# Revit family: 0052239 Lighting Fixture_Sylvania_Rana LED 600x600-DALI dimmable-4000K_Ceiling Recessed
name_source: partatom
category: Lighting Fixtures
revit_build: Autodesk Revit 2015 (Build: 20140606_1530(x64)
units: mm (PartAtom-declared; Revit-internal decimal feet)

## types (1)
- RANA LED 600 CM+P 2*LL DA 4K
    Accessory Material = Aluminum_Sylvania_RanaLED_White
    Apparent Load = 32 VA
    Assembly Code = D5020200
    Body Material = Aluminum_Sylvania_RanaLED_Silver
    Catalog Number = 0052239 RANA LED 600 CM+P 2*LL DA 4K
    Color Filter = 16777215
    Default Elevation = 0 mm  [stored 0 ft]
    Description = Provides perfect uniform light distribution greatly enhancing the lit space. Low profile for ease of installation in restricted ceiling voids. Two stage optic for optimum comfort and efficiency. UGR19 office compliant. Enclosed design reduces dust ingress and improves Lumen Maintenance Factor (LMF). 32W - 69W LED recessed luminaire. Rana LED is perfect for office lighting applications, schools, airports and general lighting applications. Available with a satin optic and micro prism diffuser. Available in recessed (600x600, 625x625, 312.5x1250 and 1200x300). Rana LED delivers high efficiency up to 6,050lm (luminaire lumen output on 4,000K version), equating to 101lm/W (total system efficiency). Available in warm white (3,000K) and neutral white (4,000K). Integrated LED solution that has the same aesthetics as a T5 or T8 diffuse luminaire. Energy efficient electronic gear including DALI and 3 hour emergency versions as standard. Long lifetime: 50,000 hours life at 70% of the original output L70. Less maintenance is required due to the long lifetime of 50,000hrs. Energy Class: A++, A+, A. LED technology provides an energy efficient solution with reduced maintenance costs. Comes complete with safety cable
    Dimming Lamp Color Temperature Shift = <None>
    Emit Shape Visible in Rendering = No
    Emit from Rectangle Length = 558 mm
    Emit from Rectangle Width = 280 mm  [stored 0.918635 ft]
    Energy Class = A++, A+, A
    Height = 46 mm  [stored 0.150919 ft]
    IK Rating = 07
    IP Rating = 20
    Lamp = Integrated LED
    Length = 592 mm  [stored 1.94226 ft]
    Life = 50 000h
    Louver Length = 558 mm
    Manufacturer = Feilo Sylvania
    Model = RANA LED 600 CM+P 2*LL DA 4K
    Photometric Web File = 0052239_RANALED600CM+P2LLDA4K-186127.ies
    Product Family = Rana LED 600x600-DALI dimmable-4000K Lamp
    Product Page URL = http://www.feilosylvania.com
    Reflector Material = Steel_Sylvania_RanaLED_Silver
    Ta Rating = 25°C
    Tilt Angle = -90.00°
    URL = http://www.feilosylvania.com
    Voltage = 230 V
    Voltage Comments = UNV (Universal Voltage; 220-240 Volt)
    Weight = 4.00 kg
    Width = 594 mm  [stored 1.94882 ft]

note: [stored X ft] marks values corroborated as IEEE doubles in the binary element streams (Revit-internal decimal feet)

## geometry (parser evidence)
native form markers: Blend x7, Sweep x5
no freeform markers — native parametric forms only
